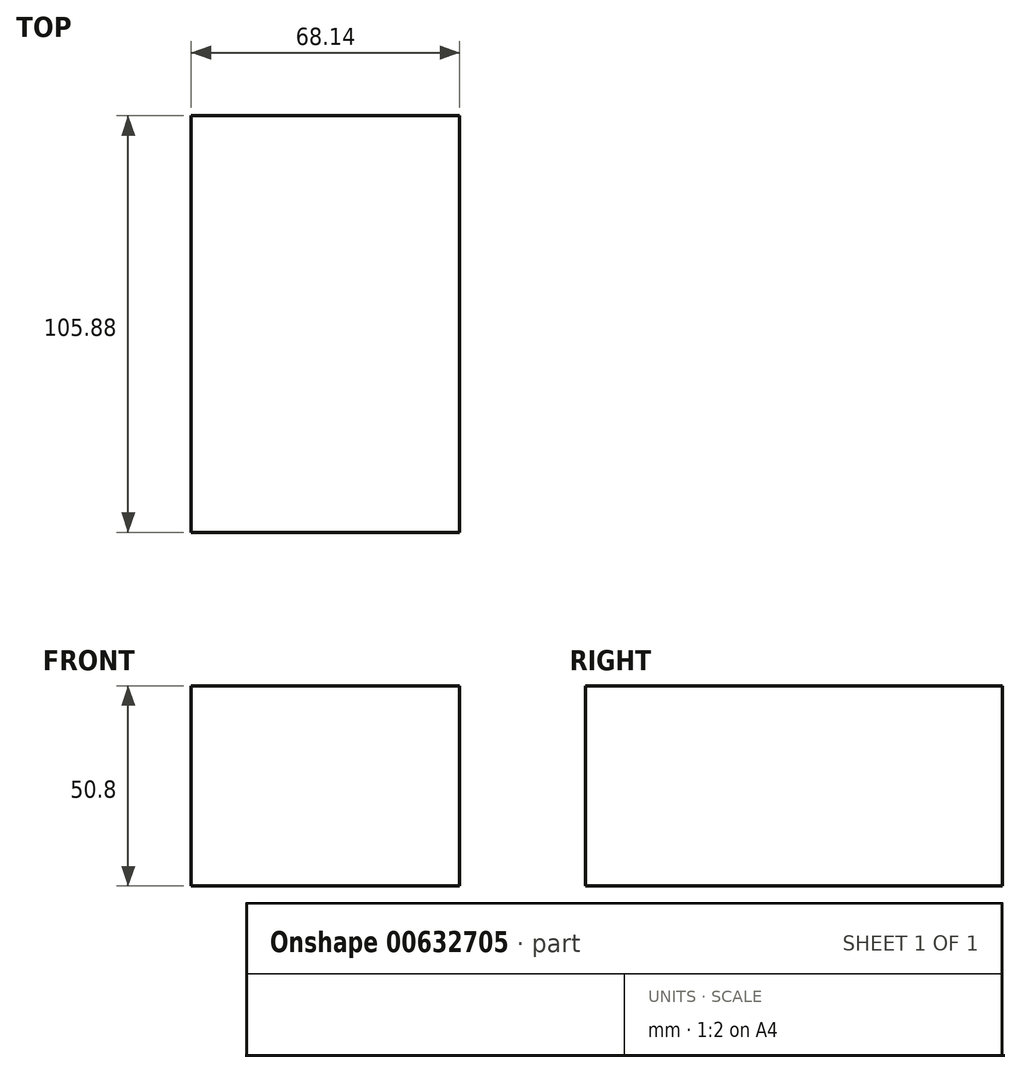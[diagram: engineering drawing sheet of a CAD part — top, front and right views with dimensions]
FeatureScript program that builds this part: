
annotation { "Feature Type Name" : "Feature", "Feature Type Description" : "" }
export const myFeature = defineFeature(function(context is Context, id is Id, definition is map)
    precondition{}
    {
        {
            var Q0;
            Q0=qCreatedBy(makeId("Top.planeOp"),FACE);
            var sketch = newSketch(context, id + "F0", { "sketchPlane" : qUnion([Q0])});
            skLineSegment(sketch, "E0.bottom", {"start": v(-34.07, 52.94) * mm, "end": v(34.07, 52.94) * mm});
            skLineSegment(sketch, "E0.top", {"start": v(-34.07, -52.94) * mm, "end": v(34.07, -52.94) * mm});
            skLineSegment(sketch, "E0.left", {"start": v(-34.07, 52.94) * mm, "end": v(-34.07, -52.94) * mm});
            skLineSegment(sketch, "E0.right", {"start": v(34.07, 52.94) * mm, "end": v(34.07, -52.94) * mm});
            skPoint(sketch, "E0.middle", {"position": v(0, 0) * mm});
            skSolve(sketch);
        }
        {
            var Q0;
            Q0 = qSketchRegion(id + "F0", true);
            extrude(context, id + "F1", {"entities" : qUnion([Q0]), "depth" : 50.8 * mm, "offsetDistance" : 25.4 * mm});
        }
    });
